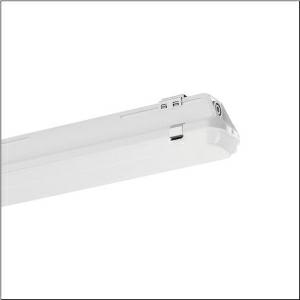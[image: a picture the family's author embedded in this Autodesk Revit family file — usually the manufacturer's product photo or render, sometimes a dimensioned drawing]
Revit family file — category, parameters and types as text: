
# Revit family: monsun_r__12_51fp109p440h_216b
name_source: partatom
category: Lighting Fixtures
units: mm (PartAtom-declared; Revit-internal decimal feet)

## family parameters
Cut with Voids When Loaded = No
Host = Face
Light Source = No
Part Type = Normal
Room Calculation Point = No
Round Connector Dimension = Use Diameter
Shared = No

## types (1)
- Monsun® 12 (1 x LED, 4120 lm, 22.9 W, 4000K)
    Apparent Load = 23 VA
    CIE Flux Codes = 47 77 93 94 100
    Color Rendering = 80
    Color Temperature = 4000K
    Default Elevation = 1800 mm
    Description = Monsun® 12, damp-proof luminaire, chain hanger, primary optical cover: enclosure, of PMMA, light emission: direct distribution, primary light characteristic: symmetric, installation type: suspended mounting, surface-mounted, horizontal mounting, vertical mounting, LED rated luminous flux: 4.120 lm, light colour: 840, colour temperature: 4000K, control gear: ECG, with terminal, 3-pole, max. 2.5mm², mains connection: 220..240V, AC, 50/60Hz, rated input power: 23W, luminaire housing, of glass-fibre reinforced polyester, uncoated, bright grey, length: 1.590 mm, width: 90 mm, height: 88mm, clip for enclosure, of stainless steel (V2A), ceiling mounting element, of stainless steel (V2A), chain hanger, of stainless steel (V2A), protection rating (complete): IP66, insulation class (complete): insulation class I (protective earthing), certification: CE, ENEC, VDE, protection symbol: D, impact resistance: IK04, permissible ambient temperature for indoor applications: -35..+40°C, standard: EN 50419, EN 60598-2-1, no direct snow, no direct sun, no direct rain, for indoor or canopied outdoor use, corresponds to IFS (International Featured Standards) requirements for safety and quality in the food industry, for animal farming (ammonia tested): for use in cowhouse, pig house, horse-stables... (not for use in poultry stables), AT max for animal farming = 40°C, packaging unit: 1 piece
    Height = 89 mm
    Lamp = 1 x LED
    Lamp Light Flux = 4120 lm
    Lamp Power = 22.9 W
    Lamp count = 1
    Length = 1590 mm
    Luminous efficacy = 180 lm/W
    Manufacturer = Siteco
    ModVariant = No
    Model = 51FP109P440H
    Mounting Place = Ceiling
    Mounting Type = Pendant
    Number of Poles = 1
    OnlyDefault = Yes
    Power Factor = 1
    Product Name = Monsun® 12
    Product group = damp-proof luminaire | ceiling pendant
    ProductGroupID = 908
    Protection Class = Protection class I
    Protection Degree = IP 66
    RLX_Detail_Level = 1
    RlxData = <blob elided: 88325 chars, md5=ea2356ff>
    Socket = socket
    Standby Power = 0 W
    System Light Flux = 4120 lm
    System Power = 23 W
    Type Comments = Product without accessories
    Type Image = l_1004748.jpg
    URL = http://relux.com
    VarID = ---
    Voltage = 0 V
    Weight = 0.00 kg
    Width = 90 mm

## geometry (parser evidence)
native form markers: Blend x4, Sweep x14
no freeform markers — native parametric forms only
